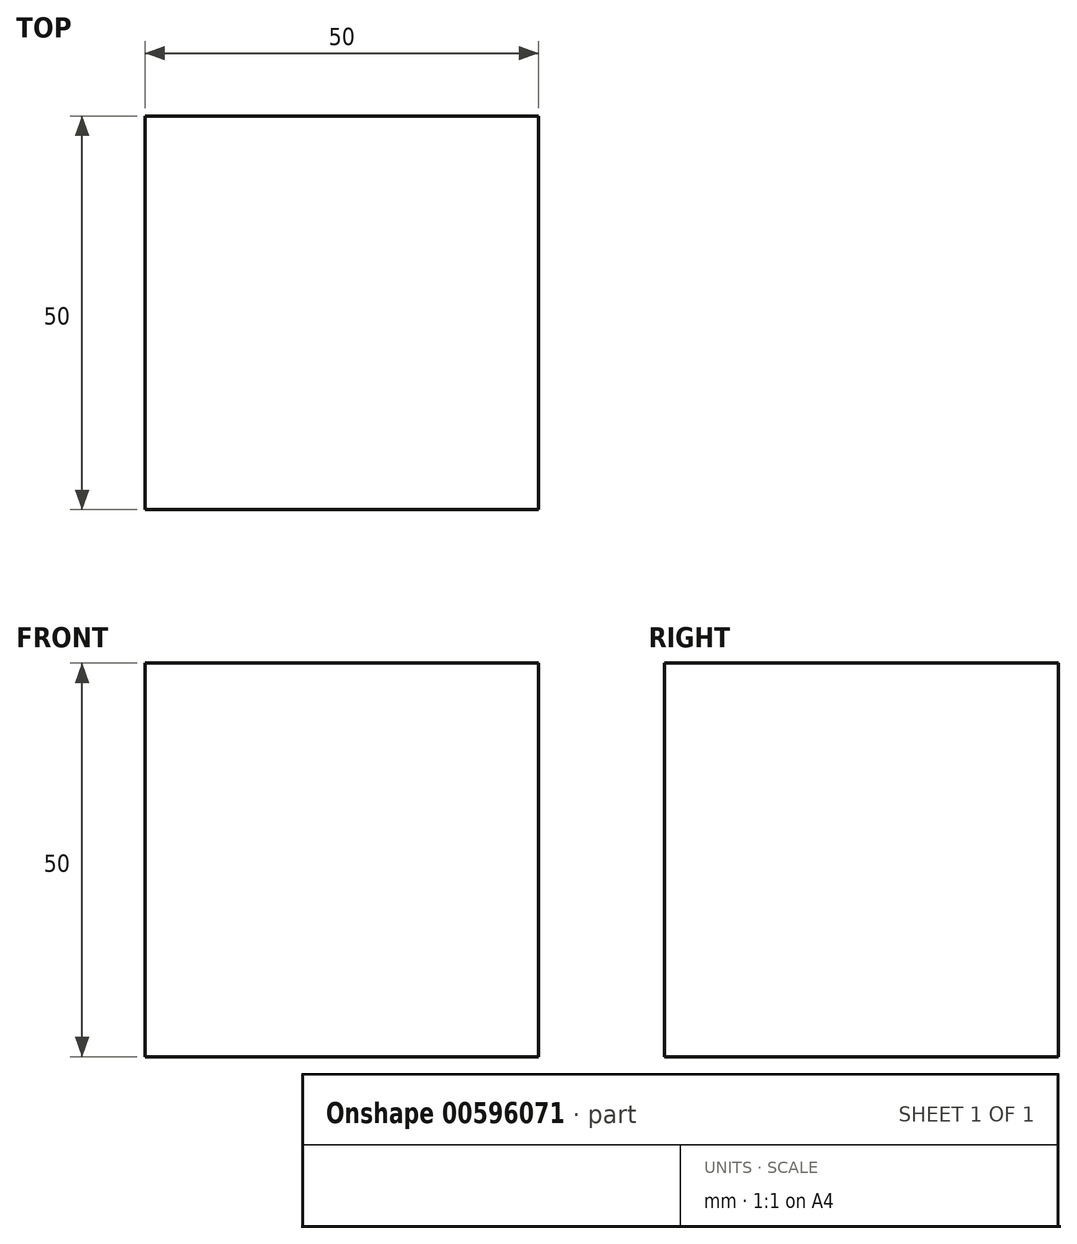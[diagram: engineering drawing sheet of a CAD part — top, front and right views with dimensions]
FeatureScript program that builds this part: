
annotation { "Feature Type Name" : "Feature", "Feature Type Description" : "" }
export const myFeature = defineFeature(function(context is Context, id is Id, definition is map)
    precondition{}
    {
        {
            var Q0;
            Q0=qCreatedBy(makeId("Top.planeOp"),FACE);
            var sketch = newSketch(context, id + "F0", { "sketchPlane" : qUnion([Q0])});
            skLineSegment(sketch, "E0.bottom", {"start": v(-21.16, 16.16) * mm, "end": v(28.84, 16.16) * mm});
            skLineSegment(sketch, "E0.top", {"start": v(-21.16, -33.84) * mm, "end": v(28.84, -33.84) * mm});
            skLineSegment(sketch, "E0.left", {"start": v(-21.16, 16.16) * mm, "end": v(-21.16, -33.84) * mm});
            skLineSegment(sketch, "E0.right", {"start": v(28.84, 16.16) * mm, "end": v(28.84, -33.84) * mm});
            skSolve(sketch);
        }
        {
            var Q0;
            Q0=makeQuery(id+"F0.imprint","IMPRINT",FACE,{"disambiguationData":[TD([[makeQuery(id+"F0.imprint","IMPRINT",EDGE,{"derivedFrom":sQuery(id+"F0.wireOp",EDGE,"E0.bottom")}),-1.0]])]});
            extrude(context, id + "F1", {"entities" : qUnion([Q0]), "depth" : 50 * mm, "offsetDistance" : 25 * mm});
        }
    });
